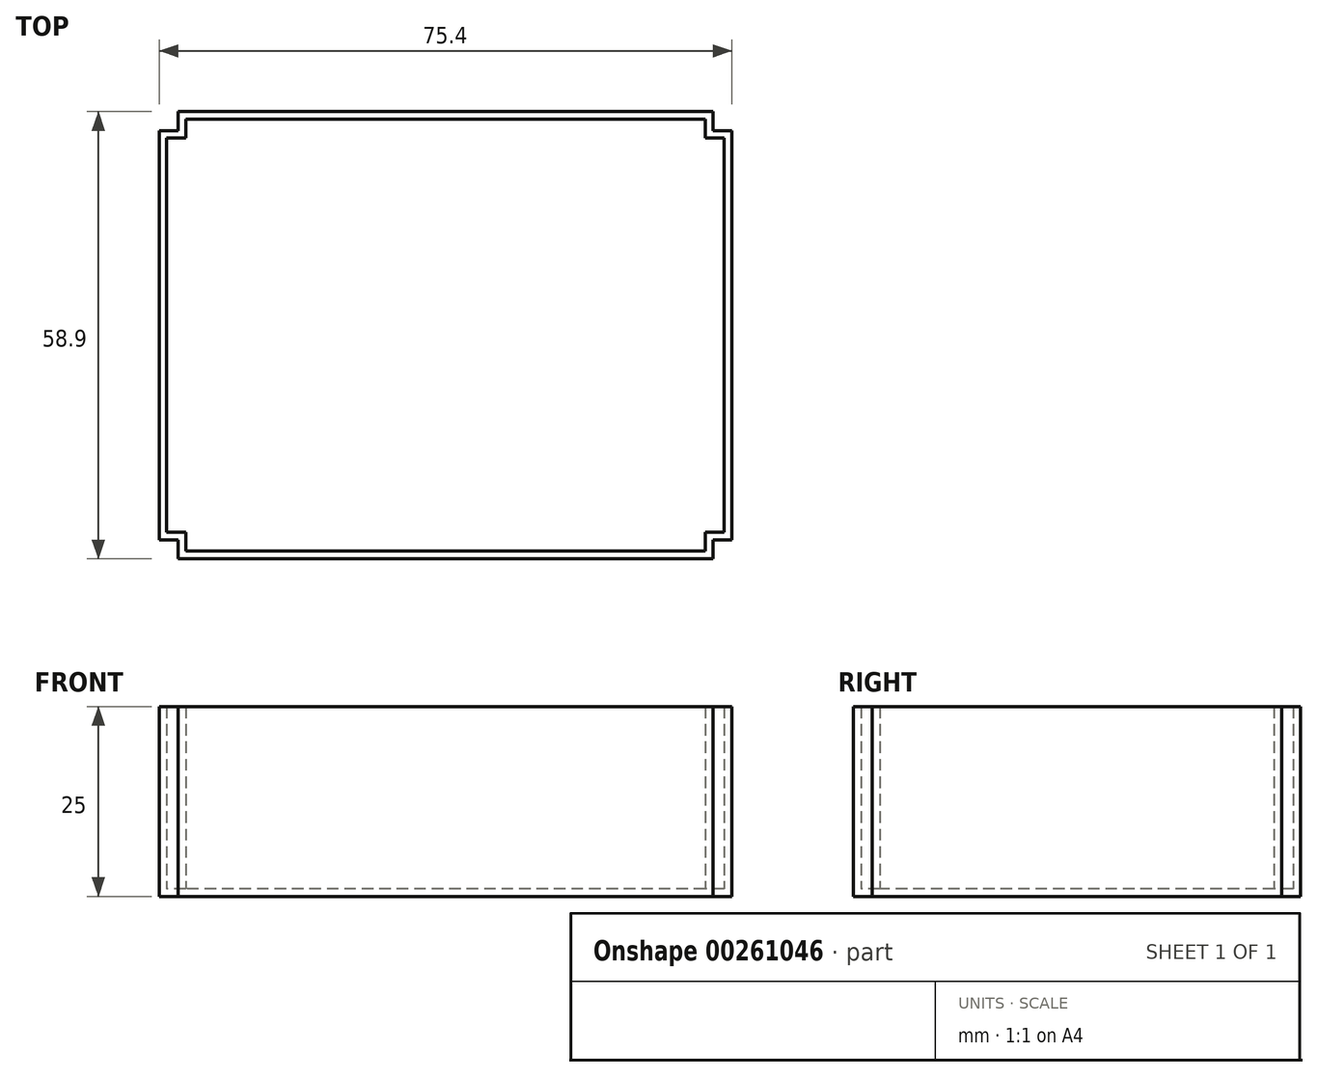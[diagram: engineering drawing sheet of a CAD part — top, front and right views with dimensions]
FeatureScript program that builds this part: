
annotation { "Feature Type Name" : "Feature", "Feature Type Description" : "" }
export const myFeature = defineFeature(function(context is Context, id is Id, definition is map)
    precondition{}
    {
        {
            var Q0;
            Q0=qCreatedBy(makeId("Top.planeOp"),FACE);
            var sketch = newSketch(context, id + "F0", { "sketchPlane" : qUnion([Q0])});
            skLineSegment(sketch, "E0.bottom", {"start": v(37.7, 29.45) * mm, "end": v(-37.7, 29.45) * mm});
            skLineSegment(sketch, "E0.top", {"start": v(37.7, -29.45) * mm, "end": v(-37.7, -29.45) * mm});
            skLineSegment(sketch, "E0.left", {"start": v(37.7, 29.45) * mm, "end": v(37.7, -29.45) * mm});
            skLineSegment(sketch, "E0.right", {"start": v(-37.7, 29.45) * mm, "end": v(-37.7, -29.45) * mm});
            skPoint(sketch, "E0.middle", {"position": v(0, 0) * mm});
            skLineSegment(sketch, "E1.bottom", {"start": v(-35.2, 31.95) * mm, "end": v(-40.2, 31.95) * mm});
            skLineSegment(sketch, "E1.top", {"start": v(-35.2, 26.95) * mm, "end": v(-40.2, 26.95) * mm});
            skLineSegment(sketch, "E1.left", {"start": v(-35.2, 31.95) * mm, "end": v(-35.2, 26.95) * mm});
            skLineSegment(sketch, "E1.right", {"start": v(-40.2, 31.95) * mm, "end": v(-40.2, 26.95) * mm});
            skPoint(sketch, "E1.middle", {"position": v(-37.7, 29.45) * mm});
            skLineSegment(sketch, "E2.bottom", {"start": v(40.2, 31.95) * mm, "end": v(35.2, 31.95) * mm});
            skLineSegment(sketch, "E2.top", {"start": v(40.2, 26.95) * mm, "end": v(35.2, 26.95) * mm});
            skLineSegment(sketch, "E2.left", {"start": v(40.2, 31.95) * mm, "end": v(40.2, 26.95) * mm});
            skLineSegment(sketch, "E2.right", {"start": v(35.2, 31.95) * mm, "end": v(35.2, 26.95) * mm});
            skPoint(sketch, "E2.middle", {"position": v(37.7, 29.45) * mm});
            skLineSegment(sketch, "E3.bottom", {"start": v(40.2, -26.95) * mm, "end": v(35.2, -26.95) * mm});
            skLineSegment(sketch, "E3.top", {"start": v(40.2, -31.95) * mm, "end": v(35.2, -31.95) * mm});
            skLineSegment(sketch, "E3.left", {"start": v(40.2, -26.95) * mm, "end": v(40.2, -31.95) * mm});
            skLineSegment(sketch, "E3.right", {"start": v(35.2, -26.95) * mm, "end": v(35.2, -31.95) * mm});
            skPoint(sketch, "E3.middle", {"position": v(37.7, -29.45) * mm});
            skLineSegment(sketch, "E4.bottom", {"start": v(-40.2, -26.95) * mm, "end": v(-35.2, -26.95) * mm});
            skLineSegment(sketch, "E4.top", {"start": v(-40.2, -31.95) * mm, "end": v(-35.2, -31.95) * mm});
            skLineSegment(sketch, "E4.left", {"start": v(-40.2, -26.95) * mm, "end": v(-40.2, -31.95) * mm});
            skLineSegment(sketch, "E4.right", {"start": v(-35.2, -26.95) * mm, "end": v(-35.2, -31.95) * mm});
            skPoint(sketch, "E4.middle", {"position": v(-37.7, -29.45) * mm});
            skSolve(sketch);
        }
        {
            var Q0;
            {var subQ0=sQuery(id+"F0.wireOp",EDGE,"E2.right");var subQ3=sQuery(id+"F0.wireOp",EDGE,"E0.bottom");var subQ4=makeQuery(id+"F0.imprint","INTERSECT",VERTEX,{"derivedFrom":[subQ3,subQ0]});Q0=makeQuery(id+"F0.imprint","IMPRINT",FACE,{"disambiguationData":[TD([[makeQuery(id+"F0.imprint","IMPRINT",EDGE,{"disambiguationData":[TD([[subQ4,-1.0]])],"derivedFrom":subQ3}),1.0]])]});}
            extrude(context, id + "F1", {"entities" : qUnion([Q0]), "depth" : 25 * mm});
        }
        {
            var Q0;
            Q0=makeQuery(id+"F1.opExtrude","CAP_FACE",FACE,{"disambiguationData":[OSD([sQuery(id+"F0.wireOp",EDGE,"E0.bottom"),sQuery(id+"F0.wireOp",EDGE,"E0.top"),sQuery(id+"F0.wireOp",EDGE,"E0.left"),sQuery(id+"F0.wireOp",EDGE,"E0.right"),sQuery(id+"F0.wireOp",EDGE,"E1.top"),sQuery(id+"F0.wireOp",EDGE,"E1.left"),sQuery(id+"F0.wireOp",EDGE,"E2.top"),sQuery(id+"F0.wireOp",EDGE,"E2.right"),sQuery(id+"F0.wireOp",EDGE,"E3.bottom"),sQuery(id+"F0.wireOp",EDGE,"E3.right"),sQuery(id+"F0.wireOp",EDGE,"E4.bottom"),sQuery(id+"F0.wireOp",EDGE,"E4.right")])],"isStart":false});
            shell(context, id + "F2", {"entities" : qUnion([Q0]), "thickness" : 1 * mm});
        }
    });
